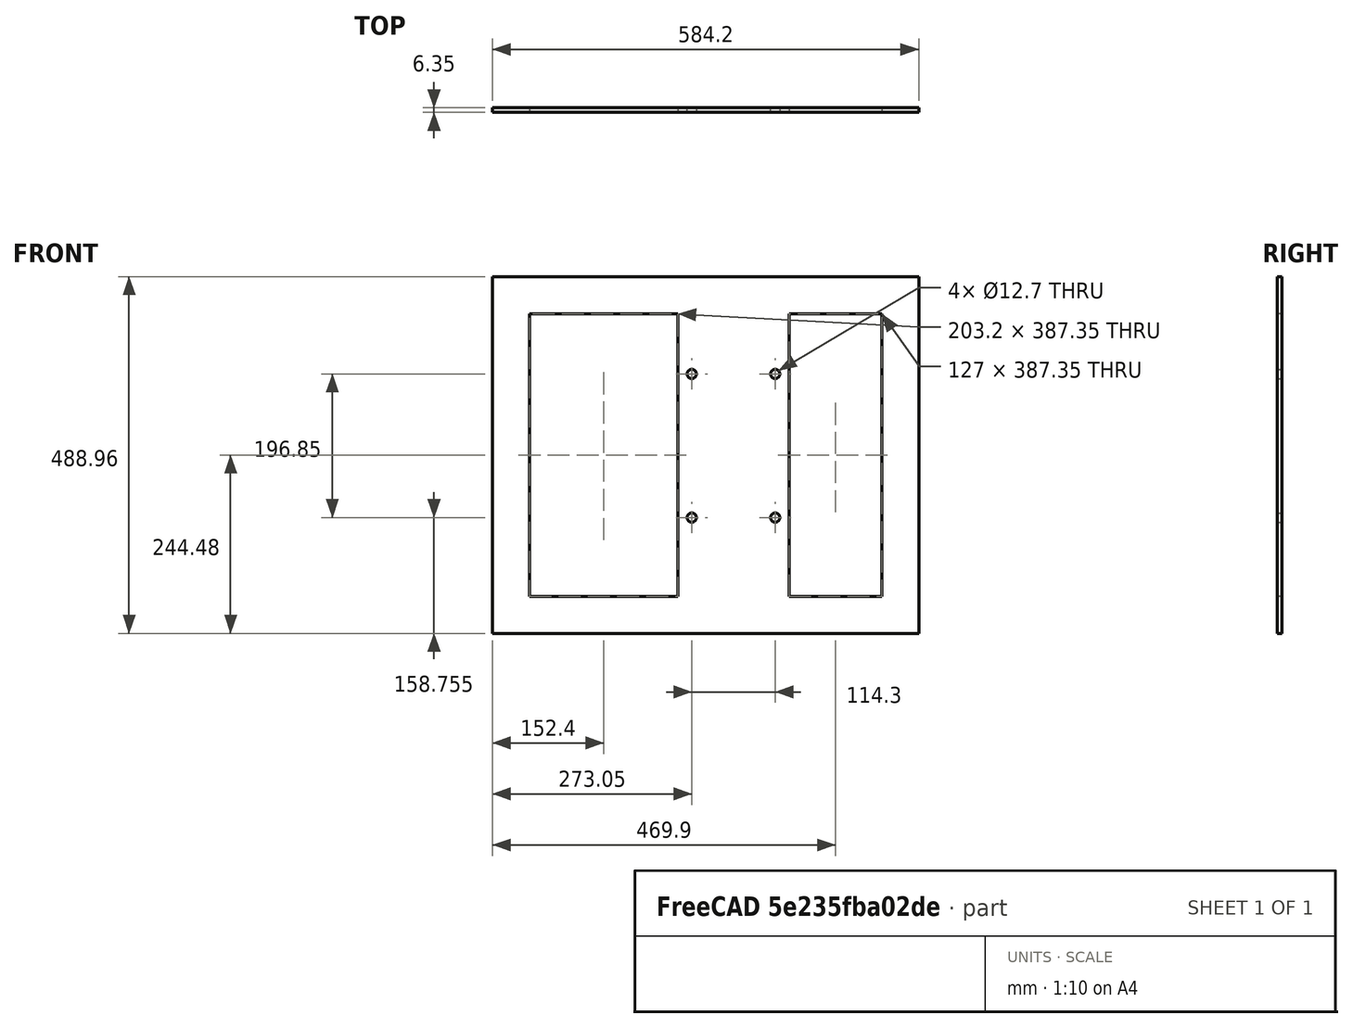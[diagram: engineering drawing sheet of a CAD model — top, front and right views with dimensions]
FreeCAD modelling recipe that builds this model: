
FCSTD DOCUMENT  (FreeCAD 0.16R6712 (Git))
Label: bottom
License: All rights reserved
LicenseURL: http://en.wikipedia.org/wiki/All_rights_reserved
objects: Sketcher::SketchObject×1, PartDesign::Pad×1
note: 3 computed .brp shape members not serialized (recipe doc carries the construction recipe); baked Part::Feature solids carry a one-line shape summary decoded from their .brp

FEATURE [Sketcher::SketchObject] Sketch003  label="Bottom mount"
  Placement = pos=(0,0,914.4) rot=(1,0,0;1.5708rad)
  sketch-geometry (31):
    g0: LineSegment StartX=-292.1 StartY=244.475 StartZ=0 EndX=292.1 EndY=244.475 EndZ=0
    g1: LineSegment StartX=292.1 StartY=244.475 StartZ=0 EndX=292.1 EndY=-244.475 EndZ=0
    g2: LineSegment StartX=292.1 StartY=-244.475 StartZ=0 EndX=-292.1 EndY=-244.475 EndZ=0
    g3: LineSegment StartX=114.3 StartY=193.675 StartZ=0 EndX=241.3 EndY=193.675 EndZ=0
    g4: LineSegment StartX=241.3 StartY=193.675 StartZ=0 EndX=241.3 EndY=-193.675 EndZ=0
    g5: LineSegment StartX=241.3 StartY=-193.675 StartZ=0 EndX=114.3 EndY=-193.675 EndZ=0
    g6: LineSegment StartX=114.3 StartY=-193.675 StartZ=0 EndX=114.3 EndY=193.675 EndZ=0
    g7: LineSegment [constr] StartX=241.3 StartY=193.675 StartZ=0 EndX=292.1 EndY=193.675 EndZ=0
    g8: LineSegment [constr] StartX=241.3 StartY=193.675 StartZ=0 EndX=241.3 EndY=244.475 EndZ=0
    g9: LineSegment [constr] StartX=241.3 StartY=-193.675 StartZ=0 EndX=241.3 EndY=-244.475 EndZ=0
    g10: LineSegment StartX=-38.1 StartY=193.675 StartZ=0 EndX=-38.1 EndY=-193.675 EndZ=0
    g11: LineSegment [constr] StartX=-38.1 StartY=193.675 StartZ=0 EndX=-38.1 EndY=244.475 EndZ=0
    g12: LineSegment [constr] StartX=114.3 StartY=193.675 StartZ=0 EndX=-38.1 EndY=193.675 EndZ=0
    g13: LineSegment StartX=-292.1 StartY=244.475 StartZ=0 EndX=-292.1 EndY=-244.475 EndZ=0
    g14: LineSegment StartX=-38.1 StartY=193.675 StartZ=0 EndX=-241.3 EndY=193.675 EndZ=0
    g15: LineSegment StartX=-38.1 StartY=-193.675 StartZ=0 EndX=-241.3 EndY=-193.675 EndZ=0
    g16: LineSegment StartX=-241.3 StartY=193.675 StartZ=0 EndX=-241.3 EndY=-193.675 EndZ=0
    g17: LineSegment [constr] StartX=114.3 StartY=193.675 StartZ=0 EndX=114.3 EndY=111.125 EndZ=0
    g18: LineSegment [constr] StartX=114.3 StartY=111.125 StartZ=0 EndX=95.25 EndY=111.125 EndZ=0
    g19: LineSegment [constr] StartX=-38.1 StartY=193.675 StartZ=0 EndX=-38.1 EndY=111.125 EndZ=0
    g20: LineSegment [constr] StartX=-38.1 StartY=111.125 StartZ=0 EndX=-19.05 EndY=111.125 EndZ=0
    g21: LineSegment [constr] StartX=114.3 StartY=-193.675 StartZ=0 EndX=114.3 EndY=-85.725 EndZ=0
    g22: LineSegment [constr] StartX=-38.1 StartY=-193.675 StartZ=0 EndX=-38.1 EndY=-85.725 EndZ=0
    g23: LineSegment [constr] StartX=-38.1 StartY=-85.725 StartZ=0 EndX=-19.05 EndY=-85.725 EndZ=0
    g24: LineSegment [constr] StartX=114.3 StartY=-85.725 StartZ=0 EndX=95.25 EndY=-85.725 EndZ=0
    g25: Circle CenterX=-19.05 CenterY=111.125 CenterZ=0 NormalX=0 NormalY=0 NormalZ=1 Radius=6.35
    g26: Circle CenterX=95.25 CenterY=111.125 CenterZ=0 NormalX=0 NormalY=0 NormalZ=1 Radius=6.35
    g27: Circle CenterX=-19.05 CenterY=-85.725 CenterZ=0 NormalX=0 NormalY=0 NormalZ=1 Radius=6.35
    g28: Circle CenterX=95.25 CenterY=-85.725 CenterZ=0 NormalX=0 NormalY=0 NormalZ=1 Radius=6.35
    g29: LineSegment [constr] StartX=-241.3 StartY=-193.675 StartZ=0 EndX=-292.1 EndY=-193.675 EndZ=0
    g30: LineSegment [constr] StartX=-241.3 StartY=-193.675 StartZ=0 EndX=-241.3 EndY=-244.475 EndZ=0
  constraints (88):
    c: Coincident(g0,g1)
    c: Coincident(g1,g2)
    c: Horizontal(g0)
    c: Vertical(g1)
    c: Symmetric(g2,g0,g-1)
    c: Equal(g2,g0)
    c: DistanceY(g2,g0) = 488.95  'width'
    c: DistanceX(g2,g2) = 584.2
    c: Coincident(g3,g4)
    c: Coincident(g4,g5)
    c: Coincident(g5,g6)
    c: Coincident(g6,g3)
    c: Horizontal(g5)
    c: Vertical(g4)
    c: Equal(g4,g6)
    c: Equal(g3,g5)
    c: Coincident(g7,g3)
    c: PointOnObject(g7,g1)
    c: Horizontal(g7)
    c: Coincident(g8,g3)
    c: PointOnObject(g8,g0)
    c: Vertical(g8)
    c: Coincident(g9,g4)
    c: PointOnObject(g9,g2)
    c: Vertical(g9)
    c: PointOnObject(g11,g0)
    c: Vertical(g11)
    c: Coincident(g12,g3)
    c: DistanceX(g12,g12) = 152.4
    c: Coincident(g13,g0)
    c: Coincident(g13,g2)
    c: Equal(g13,g1)
    c: Horizontal(g14)
    c: Horizontal(g15)
    c: Coincident(g16,g14)
    c: Coincident(g16,g15)
    c: Vertical(g16)
    c: Equal(g14,g15)
    c: Coincident(g17,g3)
    c: PointOnObject(g17,g6)
    c: DistanceY(g17,g17) = 82.55
    c: Coincident(g18,g17)
    c: Horizontal(g18)
    c: DistanceX(g18,g18) = 19.05
    c: PointOnObject(g19,g10)
    c: Vertical(g19)
    c: Equal(g17,g19)
    c: Coincident(g20,g19)
    c: Horizontal(g20)
    c: Coincident(g21,g5)
    c: PointOnObject(g21,g6)
    c: Coincident(g22,g10)
    c: PointOnObject(g22,g10)
    c: Equal(g21,g22)
    c: Coincident(g23,g22)
    c: Horizontal(g23)
    c: Coincident(g24,g21)
    c: Horizontal(g24)
    c: Equal(g18,g20)
    c: Equal(g20,g24)
    c: Equal(g24,g23)
    c: Coincident(g25,g20)
    c: Coincident(g26,g18)
    c: Coincident(g27,g23)
    c: Coincident(g28,g24)
    c: Radius(g28) = 6.35
    c: Equal(g28,g27)
    c: Equal(g27,g25)
    c: Equal(g25,g26)
    c: Coincident(g19,g11)
    c: Coincident(g11,g12)
    c: Coincident(g10,g11)
    c: Equal(g10,g16)
    c: DistanceY(g23,g20) = 196.85
    c: DistanceX(g3,g3) = 127
    c: Coincident(g29,g15)
    c: PointOnObject(g29,g13)
    c: Horizontal(g29)
    c: Coincident(g30,g15)
    c: PointOnObject(g30,g2)
    c: Vertical(g30)
    c: Equal(g7,g9)
    c: Equal(g9,g8)
    c: Equal(g8,g11)
    c: Equal(g11,g30)
    c: Equal(g30,g29)
    c: DistanceX(g29,g29) = 50.8
    c: Coincident(g10,g15)
FEATURE [PartDesign::Pad] Pad010  label="Bottom"
  Length = 6.35
  Length2 = 100
  Placement = pos=(0,0,914.4) rot=(1,0,0;1.5708rad)
  Sketch = -> Sketch003
  Type = 0
